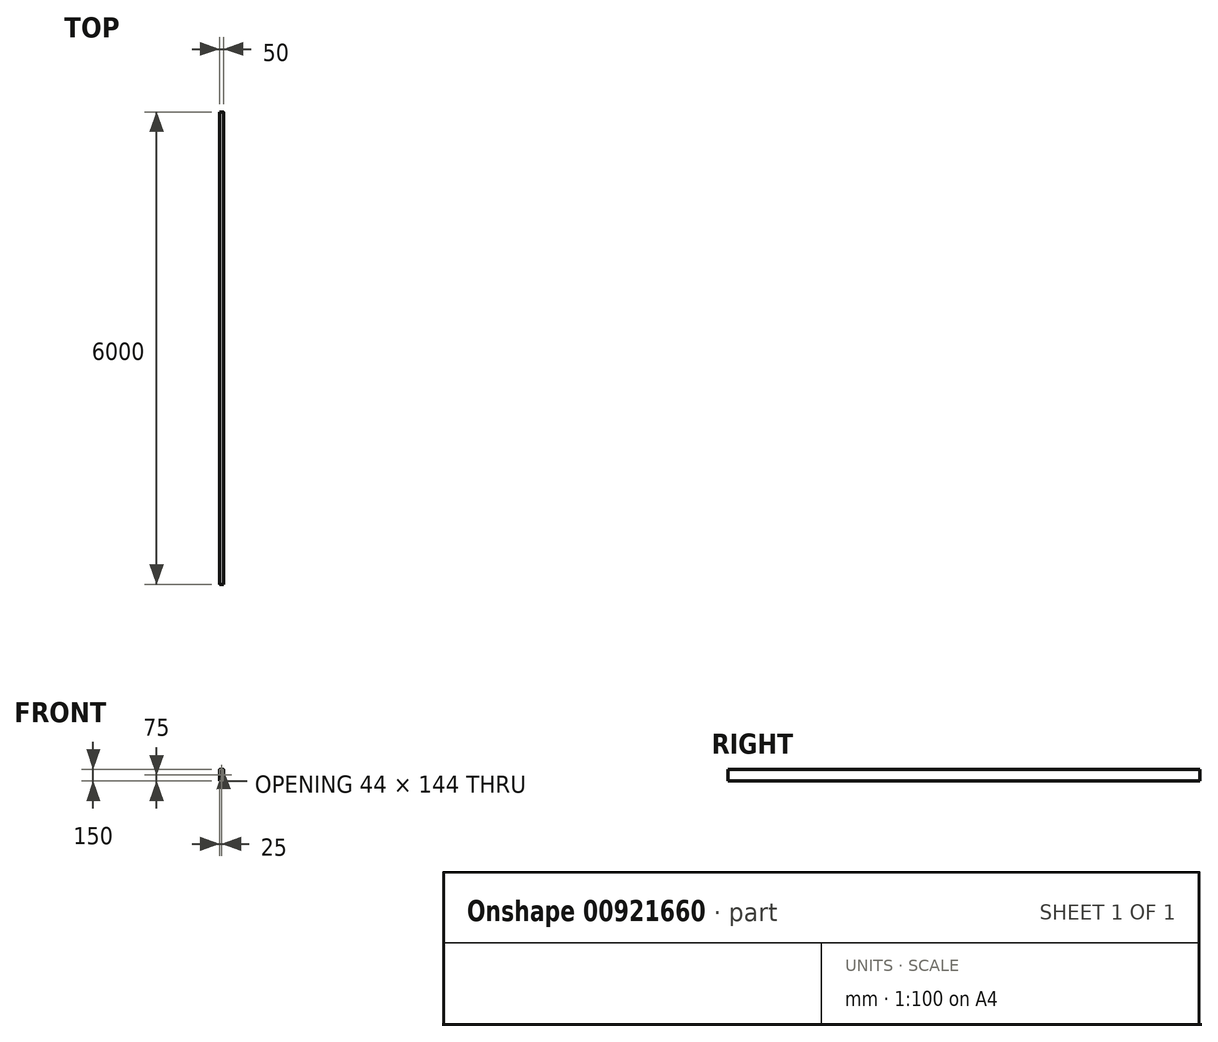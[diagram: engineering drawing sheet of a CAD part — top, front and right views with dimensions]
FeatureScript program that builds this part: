
annotation { "Feature Type Name" : "Feature", "Feature Type Description" : "" }
export const myFeature = defineFeature(function(context is Context, id is Id, definition is map)
    precondition{}
    {
        {
            var Q0;
            Q0=qCreatedBy(makeId("Front.planeOp"),FACE);
            var sketch = newSketch(context, id + "F0", { "sketchPlane" : qUnion([Q0])});
            skLineSegment(sketch, "E0.bottom", {"start": v(2.4, 0) * mm, "end": v(47.6, 0) * mm});
            skLineSegment(sketch, "E0.top", {"start": v(2.4, 150) * mm, "end": v(47.6, 150) * mm});
            skLineSegment(sketch, "E0.left", {"start": v(0, 2.4) * mm, "end": v(0, 147.6) * mm});
            skLineSegment(sketch, "E0.right", {"start": v(50, 2.4) * mm, "end": v(50, 147.6) * mm});
            skPoint(sketch, "E1.visualSharp", {"position": v(0, 150) * mm});
            skArc(sketch, "E1.filletArc", {"start": v(2.4, 150) * mm, "mid": v(0.7, 149.3) * mm, "end": v(0, 147.6) * mm});
            skPoint(sketch, "E2.visualSharp", {"position": v(50, 150) * mm});
            skArc(sketch, "E2.filletArc", {"start": v(50, 147.6) * mm, "mid": v(49.3, 149.3) * mm, "end": v(47.6, 150) * mm});
            skPoint(sketch, "E3.visualSharp", {"position": v(0, 0) * mm});
            skArc(sketch, "E3.filletArc", {"start": v(0, 2.4) * mm, "mid": v(0.7, 0.7) * mm, "end": v(2.4, 0) * mm});
            skPoint(sketch, "E4.visualSharp", {"position": v(50, 0) * mm});
            skArc(sketch, "E4.filletArc", {"start": v(47.6, 0) * mm, "mid": v(49.3, 0.7) * mm, "end": v(50, 2.4) * mm});
            skLineSegment(sketch, "E5.0", {"start": v(3, 5.4) * mm, "end": v(3, 144.6) * mm});
            skLineSegment(sketch, "E6.0", {"start": v(5.4, 147) * mm, "end": v(44.6, 147) * mm});
            skLineSegment(sketch, "E7.0", {"start": v(47, 5.4) * mm, "end": v(47, 144.6) * mm});
            skLineSegment(sketch, "E8.0", {"start": v(5.4, 3) * mm, "end": v(44.6, 3) * mm});
            skArc(sketch, "E9.filletArc", {"start": v(5.4, 147) * mm, "mid": v(3.7, 146.3) * mm, "end": v(3, 144.6) * mm});
            skArc(sketch, "E10.filletArc", {"start": v(3, 5.4) * mm, "mid": v(3.7, 3.7) * mm, "end": v(5.4, 3) * mm});
            skArc(sketch, "E11.filletArc", {"start": v(47, 144.6) * mm, "mid": v(46.3, 146.3) * mm, "end": v(44.6, 147) * mm});
            skArc(sketch, "E12.filletArc", {"start": v(44.6, 3) * mm, "mid": v(46.3, 3.7) * mm, "end": v(47, 5.4) * mm});
            skSolve(sketch);
        }
        {
            var Q0;
            Q0=qSketchRegion(id+"F0",true);
            extrude(context, id + "F1", {"entities" : qUnion([Q0]), "depth" : 6000 * mm, "offsetDistance" : 25 * mm});
        }
    });
